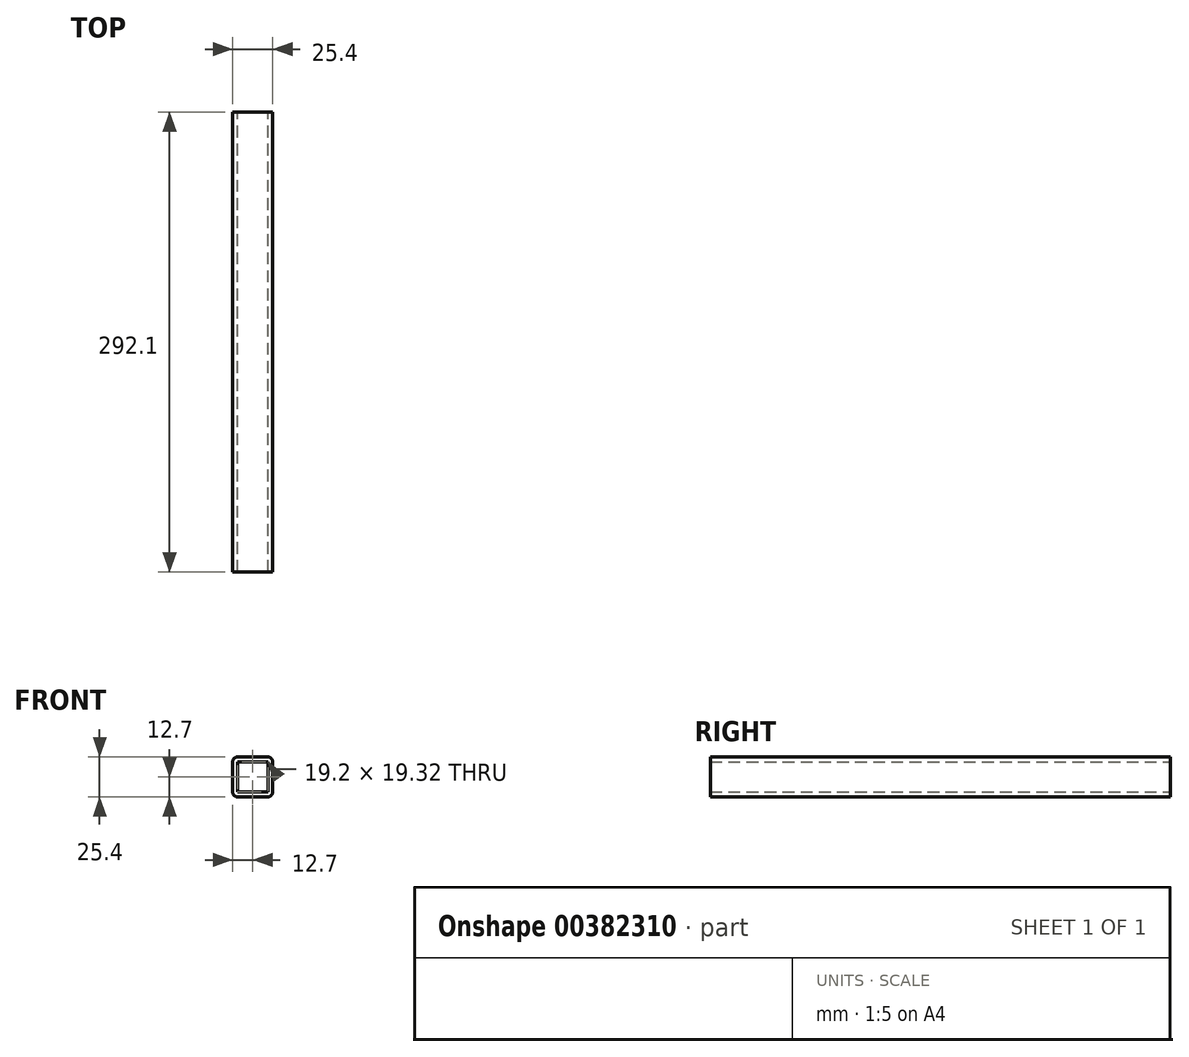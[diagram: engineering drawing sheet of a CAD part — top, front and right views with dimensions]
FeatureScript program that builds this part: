
annotation { "Feature Type Name" : "Feature", "Feature Type Description" : "" }
export const myFeature = defineFeature(function(context is Context, id is Id, definition is map)
    precondition{}
    {
        {
            var Q0;
            Q0=qCreatedBy(makeId("Front.planeOp"),FACE);
            var sketch = newSketch(context, id + "F0", { "sketchPlane" : qUnion([Q0])});
            skLineSegment(sketch, "E0.bottom", {"start": v(9.52, 12.7) * mm, "end": v(-9.53, 12.7) * mm});
            skLineSegment(sketch, "E0.top", {"start": v(9.53, -12.7) * mm, "end": v(-9.53, -12.7) * mm});
            skLineSegment(sketch, "E0.left", {"start": v(12.7, 9.52) * mm, "end": v(12.7, -9.53) * mm});
            skLineSegment(sketch, "E0.right", {"start": v(-12.7, 9.53) * mm, "end": v(-12.7, -9.53) * mm});
            skPoint(sketch, "E0.middle", {"position": v(0, 0) * mm});
            skPoint(sketch, "E1.visualSharp", {"position": v(12.7, 12.7) * mm});
            skArc(sketch, "E1.filletArc", {"start": v(12.7, 9.52) * mm, "mid": v(11.77, 11.77) * mm, "end": v(9.52, 12.7) * mm});
            skPoint(sketch, "E2.visualSharp", {"position": v(-12.7, 12.7) * mm});
            skArc(sketch, "E2.filletArc", {"start": v(-9.53, 12.7) * mm, "mid": v(-11.77, 11.77) * mm, "end": v(-12.7, 9.53) * mm});
            skPoint(sketch, "E3.visualSharp", {"position": v(-12.7, -12.7) * mm});
            skArc(sketch, "E3.filletArc", {"start": v(-12.7, -9.53) * mm, "mid": v(-11.77, -11.77) * mm, "end": v(-9.53, -12.7) * mm});
            skPoint(sketch, "E4.visualSharp", {"position": v(12.7, -12.7) * mm});
            skArc(sketch, "E4.filletArc", {"start": v(9.53, -12.7) * mm, "mid": v(11.77, -11.77) * mm, "end": v(12.7, -9.53) * mm});
            skLineSegment(sketch, "E5.bottom", {"start": v(9.6, 9.66) * mm, "end": v(-9.6, 9.66) * mm});
            skLineSegment(sketch, "E5.top", {"start": v(9.6, -9.66) * mm, "end": v(-9.6, -9.66) * mm});
            skLineSegment(sketch, "E5.left", {"start": v(9.6, 9.66) * mm, "end": v(9.6, -9.66) * mm});
            skLineSegment(sketch, "E5.right", {"start": v(-9.6, 9.66) * mm, "end": v(-9.6, -9.66) * mm});
            skSolve(sketch);
        }
        {
            var Q0;
            Q0=makeQuery(id+"F0.imprint","IMPRINT",FACE,{"disambiguationData":[TD([[makeQuery(id+"F0.imprint","IMPRINT",EDGE,{"derivedFrom":sQuery(id+"F0.wireOp",EDGE,"E0.bottom")}),1.0]])]});
            extrude(context, id + "F1", {"entities" : qUnion([Q0]), "endBound" : BoundingType.SYMMETRIC, "depth" : 292.1 * mm});
        }
    });
